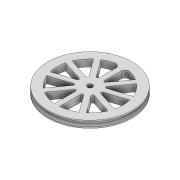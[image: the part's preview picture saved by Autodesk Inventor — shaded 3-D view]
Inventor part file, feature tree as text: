
AUTODESK INVENTOR PART (.ipt)
format: ipt  version: 2022 (Build 260153000, 153)  size: 469,504 bytes
history: native  units: mm
features: extrude x6, sketch x6, fillet x3, plane x2, projected_geometry x2
ambient origin geometry x8: Origin, YZ Plane, XZ Plane, XY Plane, X Axis, Y Axis, Z Axis, Center Point
bodies: Solid1 (feature_tree)
feature tree (19):
  extrude  "Extrusion1"  Depth=60.0mm
  extrude  "Extrusion13"  Depth=3.5mm TaperAngle=0.0deg
  plane  "Work Plane8"
  plane  "Work Plane9"
  sketch  "Sketch14"  dims[d81=3.0mm d87=4.0mm]
  sketch  "Sketch15"  dims[d88=2.0mm d92=100.0mm d94=360.0deg]
  fillet  "Fillet4"  Radius=52.0mm
  fillet  "Fillet5"  Radius=10.0mm
  extrude  "Extrusion14"  Depth=4.0mm
  extrude  "Extrusion15"  Depth=100.0mm TaperAngle=360.0deg
  extrude  "Extrusion16"  Depth=1.0mm
  extrude  "Extrusion17"  Depth=6.981317mm
  fillet  "Fillet7"  Radius=2.2mm
  sketch  "Sketch1"  dims[d0=4.1mm d2=60.0mm]
  sketch  "Sketch11"  dims[d3=4.0mm d4=3.5mm d5=0.0mm d76=52.0mm d79=10.0mm d80=0.0mm]
  sketch  "Sketch16"  dims[d96=3.0mm d97=1.0mm]
  sketch  "Sketch18"  dims[d101=-6.981317mm d102=6.981317mm d103=2.2mm d104=1.75mm d105=2.2mm d106=1.75mm d107=10.0mm d108=0.0mm d109=10.0mm d110=0.0mm d111=1.5mm d112=1.5mm d114=3.0mm d115=1.0mm d116=0.0mm d117=3.0mm d118=1.0mm d119=0.0mm d120=1.0mm]
  projected_geometry  "Projected Loop5"
  projected_geometry  "Projected Loop6"
